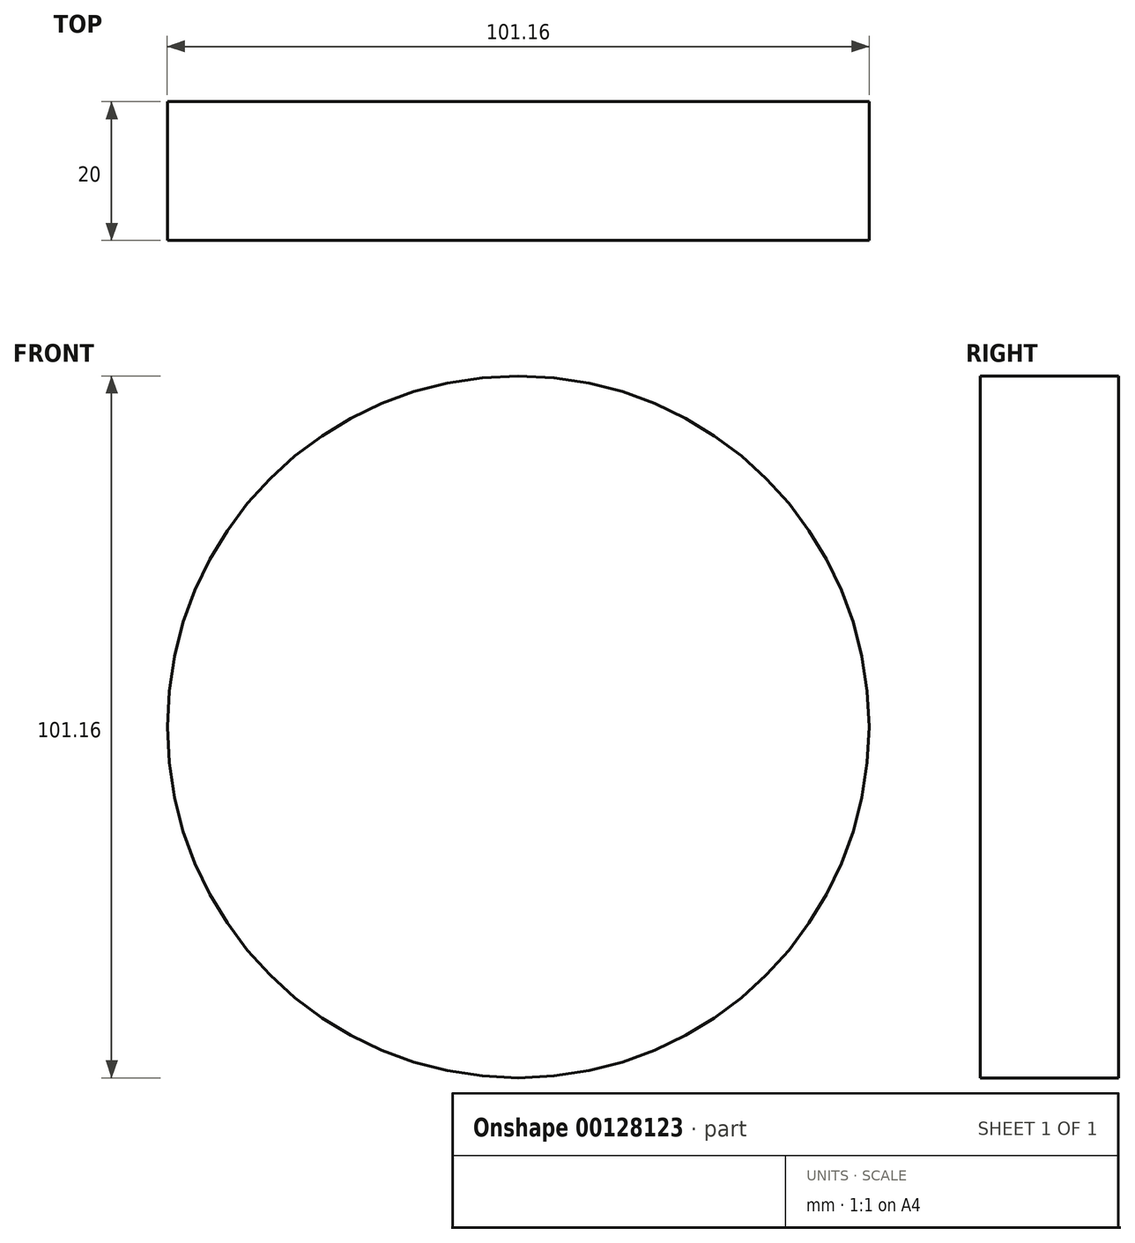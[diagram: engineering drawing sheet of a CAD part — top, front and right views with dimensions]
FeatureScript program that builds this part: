
annotation { "Feature Type Name" : "Feature", "Feature Type Description" : "" }
export const myFeature = defineFeature(function(context is Context, id is Id, definition is map)
    precondition{}
    {
        {
            var Q0;
            Q0=qCreatedBy(makeId("Front.planeOp"),FACE);
            var sketch = newSketch(context, id + "F0", { "sketchPlane" : qUnion([Q0])});
            skCircle(sketch, "E0", {"center": v(0, 0) * mm, "radius": 50.58 * mm});
            skSolve(sketch);
        }
        {
            var Q0;
            Q0 = qSketchRegion(id + "F0", true);
            extrude(context, id + "F1", {"entities" : qUnion([Q0]), "depth" : 20 * mm});
        }
    });
